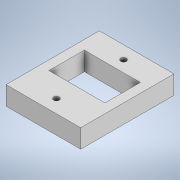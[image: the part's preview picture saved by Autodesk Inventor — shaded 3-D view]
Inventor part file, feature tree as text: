
AUTODESK INVENTOR PART (.ipt)
format: ipt  version: 2020.3 (Build 243373000, 373)  size: 233,984 bytes
history: native  units: mm
features: extrude x1, sketch x1
ambient origin geometry x8: Origin, YZ Plane, XZ Plane, XY Plane, X Axis, Y Axis, Z Axis, Center Point
bodies: Solid1 (feature_tree)
feature tree (2):
  extrude  "Extrusion1"  Depth=50.0mm
  sketch  "Sketch1"  dims[d0=40.0mm d1=50.0mm d2=3.0mm d3=3.0mm d4=10.0mm d5=0.0mm]
